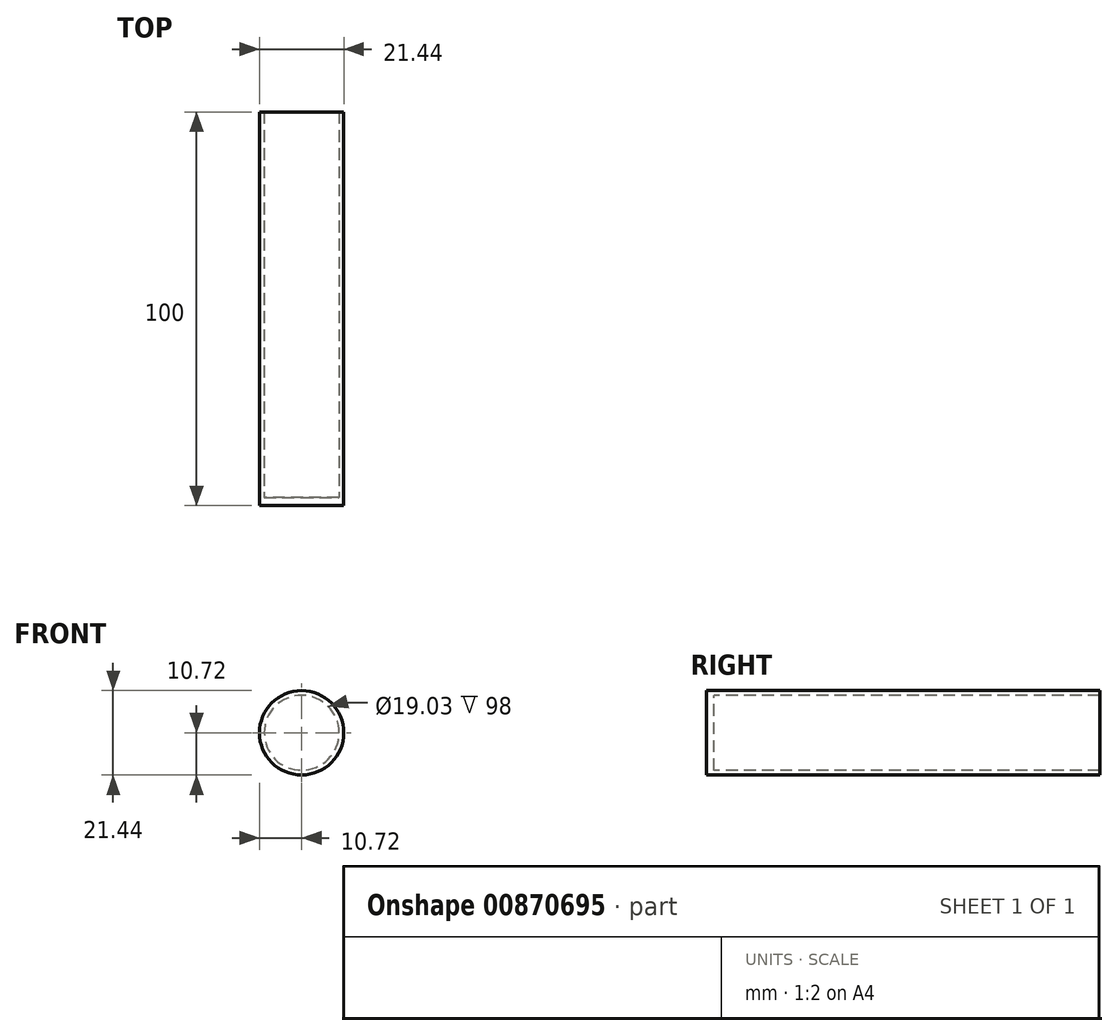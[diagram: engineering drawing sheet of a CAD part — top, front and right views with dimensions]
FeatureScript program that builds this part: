
annotation { "Feature Type Name" : "Feature", "Feature Type Description" : "" }
export const myFeature = defineFeature(function(context is Context, id is Id, definition is map)
    precondition{}
    {
        {
            var Q0;
            Q0=qCreatedBy(makeId("Front.planeOp"),FACE);
            var sketch = newSketch(context, id + "F0", { "sketchPlane" : qUnion([Q0])});
            skCircle(sketch, "E0", {"center": v(0, 0) * mm, "radius": 10.71 * mm});
            skCircle(sketch, "E1", {"center": v(0, 0) * mm, "radius": 9.52 * mm});
            skSolve(sketch);
        }
        {
            var Q0;
            Q0 = qSketchRegion(id + "F0", true);
            extrude(context, id + "F1", {"entities" : qUnion([Q0]), "oppositeDirection" : true, "depth" : 100 * mm, "offsetDistance" : 25 * mm});
        }
        {
            var Q0;
            Q0=makeQuery(id+"F0.imprint","IMPRINT",FACE,{"disambiguationData":[TD([[makeQuery(id+"F0.imprint","IMPRINT",EDGE,{"derivedFrom":sQuery(id+"F0.wireOp",EDGE,"E1")}),1.0]])]});
            extrude(context, id + "F2", {"entities" : qUnion([Q0]), "operationType" : NewBodyOperationType.ADD, "oppositeDirection" : true, "depth" : 2 * mm, "offsetDistance" : 25 * mm});
        }
    });
